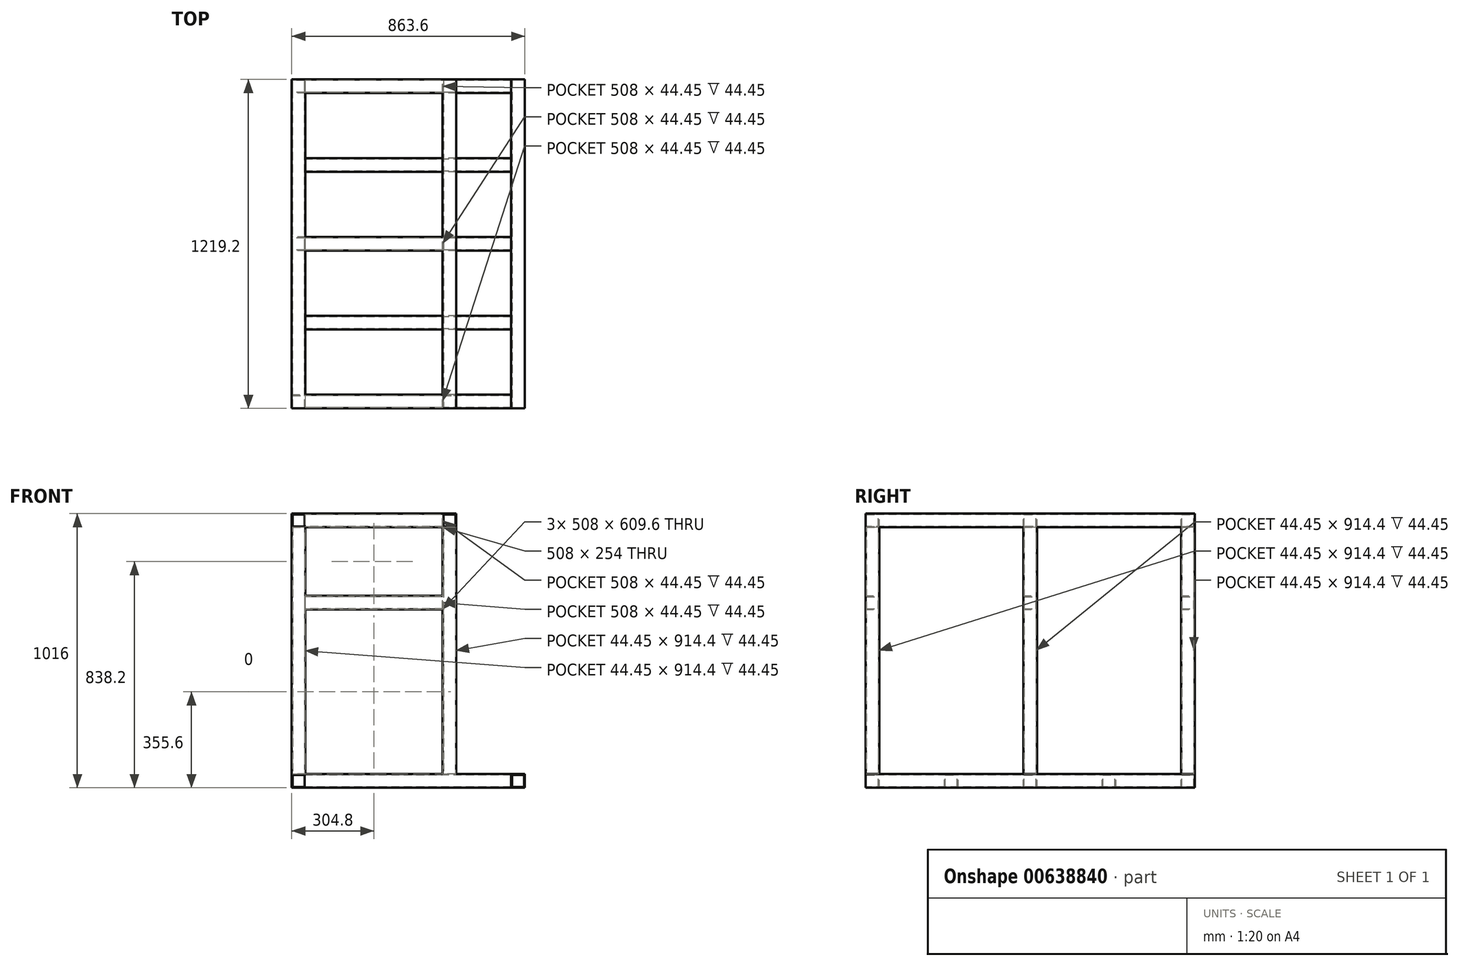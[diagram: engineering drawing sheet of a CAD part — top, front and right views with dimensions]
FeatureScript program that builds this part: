
annotation { "Feature Type Name" : "Feature", "Feature Type Description" : "" }
export const myFeature = defineFeature(function(context is Context, id is Id, definition is map)
    precondition{}
    {
        {
            var Q0;
            Q0=qCreatedBy(makeId("Front.planeOp"),FACE);
            var sketch = newSketch(context, id + "F0", { "sketchPlane" : qUnion([Q0])});
            skLineSegment(sketch, "E0.bottom", {"start": v(0, 0) * mm, "end": v(50.8, 0) * mm});
            skLineSegment(sketch, "E0.top", {"start": v(0, 50.8) * mm, "end": v(50.8, 50.8) * mm});
            skLineSegment(sketch, "E0.left", {"start": v(0, 0) * mm, "end": v(0, 50.8) * mm});
            skLineSegment(sketch, "E0.right", {"start": v(50.8, 0) * mm, "end": v(50.8, 50.8) * mm});
            skLineSegment(sketch, "E1.bottom", {"start": v(3.18, 3.17) * mm, "end": v(47.63, 3.17) * mm});
            skLineSegment(sketch, "E1.top", {"start": v(3.17, 47.63) * mm, "end": v(47.62, 47.63) * mm});
            skLineSegment(sketch, "E1.left", {"start": v(3.18, 3.18) * mm, "end": v(3.17, 47.63) * mm});
            skLineSegment(sketch, "E1.right", {"start": v(47.63, 3.18) * mm, "end": v(47.62, 47.63) * mm});
            skSolve(sketch);
        }
        {
            var Q0;
            Q0 = qSketchRegion(id + "F0", true);
            extrude(context, id + "F1", {"entities" : qUnion([Q0]), "depth" : 1219.2 * mm, "offsetDistance" : 25.4 * mm});
        }
        {
            var Q0;
            Q0=makeQuery(id+"F1.opExtrude","SWEPT_FACE",FACE,{"disambiguationData":[OSD([sQuery(id+"F0.wireOp",EDGE,"E0.right")])]});
            var sketch = newSketch(context, id + "F2", { "sketchPlane" : qUnion([Q0])});
            skLineSegment(sketch, "E2.bottom", {"start": v(-1219.2, 0) * mm, "end": v(-1168.4, 0) * mm});
            skLineSegment(sketch, "E2.top", {"start": v(-1219.2, 50.8) * mm, "end": v(-1168.4, 50.8) * mm});
            skLineSegment(sketch, "E2.left", {"start": v(-1219.2, 0) * mm, "end": v(-1219.2, 50.8) * mm});
            skLineSegment(sketch, "E2.right", {"start": v(-1168.4, 0) * mm, "end": v(-1168.4, 50.8) * mm});
            skLineSegment(sketch, "E3.0", {"start": v(-1171.57, 3.17) * mm, "end": v(-1171.57, 47.63) * mm});
            skLineSegment(sketch, "E3.1", {"start": v(-1216.03, 3.17) * mm, "end": v(-1171.57, 3.17) * mm});
            skLineSegment(sketch, "E3.2", {"start": v(-1216.03, 3.17) * mm, "end": v(-1216.03, 47.63) * mm});
            skLineSegment(sketch, "E3.3", {"start": v(-1216.03, 47.63) * mm, "end": v(-1171.57, 47.63) * mm});
            skLineSegment(sketch, "E4.direction1", {"start": v(-1219.2, 0) * mm, "end": v(-927.1, 0) * mm, "construction": true});
            skLineSegment(sketch, "E5.0.1.0", {"start": v(-923.93, 47.63) * mm, "end": v(-879.48, 47.63) * mm});
            skLineSegment(sketch, "E5.3.1.0", {"start": v(-923.93, 3.17) * mm, "end": v(-923.93, 47.63) * mm});
            skLineSegment(sketch, "E5.6.1.0", {"start": v(-923.93, 3.17) * mm, "end": v(-879.48, 3.17) * mm});
            skLineSegment(sketch, "E5.9.1.0", {"start": v(-927.1, 50.8) * mm, "end": v(-876.3, 50.8) * mm});
            skLineSegment(sketch, "E5.12.1.0", {"start": v(-927.1, 0) * mm, "end": v(-876.3, 0) * mm});
            skLineSegment(sketch, "E5.15.1.0", {"start": v(-879.48, 3.17) * mm, "end": v(-879.48, 47.63) * mm});
            skLineSegment(sketch, "E5.18.1.0", {"start": v(-876.3, 0) * mm, "end": v(-876.3, 50.8) * mm});
            skLineSegment(sketch, "E5.21.1.0", {"start": v(-927.1, 0) * mm, "end": v(-927.1, 50.8) * mm});
            skLineSegment(sketch, "E6.0.2.0", {"start": v(-631.83, 47.63) * mm, "end": v(-587.38, 47.63) * mm});
            skLineSegment(sketch, "E6.3.2.0", {"start": v(-631.83, 3.17) * mm, "end": v(-631.83, 47.63) * mm});
            skLineSegment(sketch, "E6.6.2.0", {"start": v(-631.83, 3.17) * mm, "end": v(-587.38, 3.17) * mm});
            skLineSegment(sketch, "E6.9.2.0", {"start": v(-635, 50.8) * mm, "end": v(-584.2, 50.8) * mm});
            skLineSegment(sketch, "E6.12.2.0", {"start": v(-635, 0) * mm, "end": v(-584.2, 0) * mm});
            skLineSegment(sketch, "E6.15.2.0", {"start": v(-587.38, 3.17) * mm, "end": v(-587.38, 47.63) * mm});
            skLineSegment(sketch, "E6.18.2.0", {"start": v(-584.2, 0) * mm, "end": v(-584.2, 50.8) * mm});
            skLineSegment(sketch, "E6.21.2.0", {"start": v(-635, 0) * mm, "end": v(-635, 50.8) * mm});
            skLineSegment(sketch, "E6.0.3.0", {"start": v(-339.73, 47.63) * mm, "end": v(-295.27, 47.63) * mm});
            skLineSegment(sketch, "E6.3.3.0", {"start": v(-339.73, 3.17) * mm, "end": v(-339.73, 47.63) * mm});
            skLineSegment(sketch, "E6.6.3.0", {"start": v(-339.73, 3.17) * mm, "end": v(-295.27, 3.17) * mm});
            skLineSegment(sketch, "E6.9.3.0", {"start": v(-342.9, 50.8) * mm, "end": v(-292.1, 50.8) * mm});
            skLineSegment(sketch, "E6.12.3.0", {"start": v(-342.9, 0) * mm, "end": v(-292.1, 0) * mm});
            skLineSegment(sketch, "E6.15.3.0", {"start": v(-295.27, 3.17) * mm, "end": v(-295.27, 47.63) * mm});
            skLineSegment(sketch, "E6.18.3.0", {"start": v(-292.1, 0) * mm, "end": v(-292.1, 50.8) * mm});
            skLineSegment(sketch, "E6.21.3.0", {"start": v(-342.9, 0) * mm, "end": v(-342.9, 50.8) * mm});
            skLineSegment(sketch, "E7.0.4.0", {"start": v(-47.63, 47.63) * mm, "end": v(-3.17, 47.63) * mm});
            skLineSegment(sketch, "E7.3.4.0", {"start": v(-47.63, 3.17) * mm, "end": v(-47.63, 47.63) * mm});
            skLineSegment(sketch, "E7.6.4.0", {"start": v(-47.63, 3.17) * mm, "end": v(-3.17, 3.17) * mm});
            skLineSegment(sketch, "E7.9.4.0", {"start": v(-50.8, 50.8) * mm, "end": v(0, 50.8) * mm});
            skLineSegment(sketch, "E7.12.4.0", {"start": v(-50.8, 0) * mm, "end": v(0, 0) * mm});
            skLineSegment(sketch, "E7.15.4.0", {"start": v(-3.17, 3.17) * mm, "end": v(-3.17, 47.63) * mm});
            skLineSegment(sketch, "E7.18.4.0", {"start": v(0, 0) * mm, "end": v(0, 50.8) * mm});
            skLineSegment(sketch, "E7.21.4.0", {"start": v(-50.8, 0) * mm, "end": v(-50.8, 50.8) * mm});
            skSolve(sketch);
        }
        {
            var Q0;
            Q0 = qSketchRegion(id + "F2", true);
            extrude(context, id + "F3", {"entities" : qUnion([Q0]), "operationType" : NewBodyOperationType.ADD, "depth" : 762 * mm, "offsetDistance" : 25.4 * mm});
        }
        {
            var Q0;
            Q0=makeQuery(id+"F3.boolean.opBoolean","MERGE",FACE,{"derivedFrom":[makeQuery(id+"F1.opExtrude","CAP_FACE",FACE,{"disambiguationData":[OSD([sQuery(id+"F0.wireOp",EDGE,"E0.bottom"),sQuery(id+"F0.wireOp",EDGE,"E0.top"),sQuery(id+"F0.wireOp",EDGE,"E0.left"),sQuery(id+"F0.wireOp",EDGE,"E0.right"),sQuery(id+"F0.wireOp",EDGE,"E1.bottom"),sQuery(id+"F0.wireOp",EDGE,"E1.top"),sQuery(id+"F0.wireOp",EDGE,"E1.left"),sQuery(id+"F0.wireOp",EDGE,"E1.right")])],"isStart":false}),makeQuery(id+"F3.opExtrude","SWEPT_FACE",FACE,{"disambiguationData":[OSD([sQuery(id+"F2.wireOp",EDGE,"E2.left")])]})]});
            var sketch = newSketch(context, id + "F4", { "sketchPlane" : qUnion([Q0])});
            skLineSegment(sketch, "E8.bottom", {"start": v(812.8, 0) * mm, "end": v(863.6, 0) * mm});
            skLineSegment(sketch, "E8.top", {"start": v(812.8, 50.8) * mm, "end": v(863.6, 50.8) * mm});
            skLineSegment(sketch, "E8.left", {"start": v(812.8, 0) * mm, "end": v(812.8, 50.8) * mm});
            skLineSegment(sketch, "E8.right", {"start": v(863.6, 0) * mm, "end": v(863.6, 50.8) * mm});
            skLineSegment(sketch, "E9.0", {"start": v(815.98, 3.18) * mm, "end": v(860.42, 3.18) * mm});
            skLineSegment(sketch, "E9.1", {"start": v(815.98, 3.18) * mm, "end": v(815.98, 47.62) * mm});
            skLineSegment(sketch, "E9.2", {"start": v(815.98, 47.62) * mm, "end": v(860.42, 47.62) * mm});
            skLineSegment(sketch, "E9.3", {"start": v(860.42, 3.18) * mm, "end": v(860.42, 47.62) * mm});
            skSolve(sketch);
        }
        {
            var Q0;
            Q0 = qSketchRegion(id + "F4", true);
            extrude(context, id + "F5", {"entities" : qUnion([Q0]), "oppositeDirection" : true, "depth" : 1219.2 * mm, "offsetDistance" : 25.4 * mm});
        }
        {
            var Q0;
            Q0=makeQuery(id+"F3.boolean.opBoolean","MERGE",FACE,{"derivedFrom":[makeQuery(id+"F1.opExtrude","SWEPT_FACE",FACE,{"disambiguationData":[OSD([sQuery(id+"F0.wireOp",EDGE,"E0.top")])]}),makeQuery(id+"F3.opExtrude","SWEPT_FACE",FACE,{"disambiguationData":[OSD([sQuery(id+"F2.wireOp",EDGE,"E2.top")])]}),makeQuery(id+"F3.opExtrude","SWEPT_FACE",FACE,{"disambiguationData":[OSD([sQuery(id+"F2.wireOp",EDGE,"E5.9.1.0")])]}),makeQuery(id+"F3.opExtrude","SWEPT_FACE",FACE,{"disambiguationData":[OSD([sQuery(id+"F2.wireOp",EDGE,"E6.9.2.0")])]}),makeQuery(id+"F3.opExtrude","SWEPT_FACE",FACE,{"disambiguationData":[OSD([sQuery(id+"F2.wireOp",EDGE,"E6.9.3.0")])]}),makeQuery(id+"F3.opExtrude","SWEPT_FACE",FACE,{"disambiguationData":[OSD([sQuery(id+"F2.wireOp",EDGE,"E7.9.4.0")])]})]});
            var sketch = newSketch(context, id + "F6", { "sketchPlane" : qUnion([Q0])});
            skLineSegment(sketch, "E10.bottom", {"start": v(0, -1219.2) * mm, "end": v(50.8, -1219.2) * mm});
            skLineSegment(sketch, "E10.top", {"start": v(0, -1168.4) * mm, "end": v(50.8, -1168.4) * mm});
            skLineSegment(sketch, "E10.left", {"start": v(0, -1219.2) * mm, "end": v(0, -1168.4) * mm});
            skLineSegment(sketch, "E10.right", {"start": v(50.8, -1219.2) * mm, "end": v(50.8, -1168.4) * mm});
            skLineSegment(sketch, "E11.bottom", {"start": v(50.8, -50.8) * mm, "end": v(0, -50.8) * mm});
            skLineSegment(sketch, "E11.top", {"start": v(50.8, 0) * mm, "end": v(0, 0) * mm});
            skLineSegment(sketch, "E11.left", {"start": v(50.8, -50.8) * mm, "end": v(50.8, 0) * mm});
            skLineSegment(sketch, "E11.right", {"start": v(0, -50.8) * mm, "end": v(0, 0) * mm});
            skLineSegment(sketch, "E12.bottom", {"start": v(50.8, -635) * mm, "end": v(0, -635) * mm});
            skLineSegment(sketch, "E12.top", {"start": v(50.8, -584.2) * mm, "end": v(0, -584.2) * mm});
            skLineSegment(sketch, "E12.left", {"start": v(50.8, -635) * mm, "end": v(50.8, -584.2) * mm});
            skLineSegment(sketch, "E12.right", {"start": v(0, -635) * mm, "end": v(0, -584.2) * mm});
            skLineSegment(sketch, "E13.0", {"start": v(3.17, -1171.58) * mm, "end": v(47.63, -1171.58) * mm});
            skLineSegment(sketch, "E13.1", {"start": v(3.17, -1216.03) * mm, "end": v(3.17, -1171.58) * mm});
            skLineSegment(sketch, "E13.2", {"start": v(3.17, -1216.03) * mm, "end": v(47.63, -1216.03) * mm});
            skLineSegment(sketch, "E13.3", {"start": v(47.63, -1216.03) * mm, "end": v(47.63, -1171.58) * mm});
            skLineSegment(sketch, "E14.0", {"start": v(3.18, -631.83) * mm, "end": v(3.17, -587.38) * mm});
            skLineSegment(sketch, "E14.1", {"start": v(47.63, -631.83) * mm, "end": v(3.18, -631.83) * mm});
            skLineSegment(sketch, "E14.2", {"start": v(47.63, -631.83) * mm, "end": v(47.62, -587.38) * mm});
            skLineSegment(sketch, "E14.3", {"start": v(47.62, -587.38) * mm, "end": v(3.17, -587.38) * mm});
            skLineSegment(sketch, "E15.0", {"start": v(47.63, -47.63) * mm, "end": v(3.18, -47.63) * mm});
            skLineSegment(sketch, "E15.1", {"start": v(47.63, -47.63) * mm, "end": v(47.62, -3.17) * mm});
            skLineSegment(sketch, "E15.2", {"start": v(47.62, -3.17) * mm, "end": v(3.17, -3.17) * mm});
            skLineSegment(sketch, "E15.3", {"start": v(3.18, -47.63) * mm, "end": v(3.17, -3.18) * mm});
            skLineSegment(sketch, "E16.1.0.0", {"start": v(558.8, -1219.2) * mm, "end": v(609.6, -1219.2) * mm});
            skLineSegment(sketch, "E16.1.0.1", {"start": v(561.97, -1216.03) * mm, "end": v(606.42, -1216.03) * mm});
            skLineSegment(sketch, "E16.1.0.2", {"start": v(609.6, 0) * mm, "end": v(558.8, 0) * mm});
            skLineSegment(sketch, "E16.1.0.3", {"start": v(606.42, -587.38) * mm, "end": v(561.97, -587.38) * mm});
            skLineSegment(sketch, "E16.1.0.4", {"start": v(606.42, -631.83) * mm, "end": v(561.97, -631.83) * mm});
            skLineSegment(sketch, "E16.1.0.5", {"start": v(606.42, -3.17) * mm, "end": v(561.97, -3.17) * mm});
            skLineSegment(sketch, "E16.1.0.6", {"start": v(609.6, -635) * mm, "end": v(609.6, -584.2) * mm});
            skLineSegment(sketch, "E16.1.0.7", {"start": v(609.6, -584.2) * mm, "end": v(558.8, -584.2) * mm});
            skLineSegment(sketch, "E16.1.0.8", {"start": v(609.6, -635) * mm, "end": v(558.8, -635) * mm});
            skLineSegment(sketch, "E16.1.0.9", {"start": v(558.8, -1168.4) * mm, "end": v(609.6, -1168.4) * mm});
            skLineSegment(sketch, "E16.1.0.10", {"start": v(609.6, -50.8) * mm, "end": v(558.8, -50.8) * mm});
            skLineSegment(sketch, "E16.1.0.11", {"start": v(561.97, -1171.58) * mm, "end": v(606.42, -1171.58) * mm});
            skLineSegment(sketch, "E16.1.0.12", {"start": v(606.42, -1216.03) * mm, "end": v(606.42, -1171.58) * mm});
            skLineSegment(sketch, "E16.1.0.13", {"start": v(558.8, -1219.2) * mm, "end": v(558.8, -1168.4) * mm});
            skLineSegment(sketch, "E16.1.0.14", {"start": v(609.6, -1219.2) * mm, "end": v(609.6, -1168.4) * mm});
            skLineSegment(sketch, "E16.1.0.15", {"start": v(609.6, -50.8) * mm, "end": v(609.6, 0) * mm});
            skLineSegment(sketch, "E16.1.0.16", {"start": v(558.8, -50.8) * mm, "end": v(558.8, 0) * mm});
            skLineSegment(sketch, "E16.1.0.17", {"start": v(561.97, -1216.03) * mm, "end": v(561.97, -1171.58) * mm});
            skLineSegment(sketch, "E16.1.0.18", {"start": v(606.42, -47.63) * mm, "end": v(606.42, -3.17) * mm});
            skLineSegment(sketch, "E16.1.0.19", {"start": v(561.97, -47.63) * mm, "end": v(561.97, -3.18) * mm});
            skLineSegment(sketch, "E16.1.0.20", {"start": v(606.42, -631.83) * mm, "end": v(606.42, -587.38) * mm});
            skLineSegment(sketch, "E16.1.0.21", {"start": v(606.42, -47.63) * mm, "end": v(561.97, -47.63) * mm});
            skLineSegment(sketch, "E16.1.0.22", {"start": v(558.8, -635) * mm, "end": v(558.8, -584.2) * mm});
            skLineSegment(sketch, "E16.1.0.23", {"start": v(561.97, -631.83) * mm, "end": v(561.97, -587.38) * mm});
            skLineSegment(sketch, "E16.direction1", {"start": v(0, -1219.2) * mm, "end": v(558.8, -1219.2) * mm, "construction": true});
            skSolve(sketch);
        }
        {
            var Q0;
            Q0 = qSketchRegion(id + "F6", true);
            extrude(context, id + "F7", {"entities" : qUnion([Q0]), "operationType" : NewBodyOperationType.ADD, "depth" : 914.4 * mm, "offsetDistance" : 25.4 * mm});
        }
        {
            var Q0;
            Q0=makeQuery(id+"F7.boolean.opBoolean","MERGE",FACE,{"derivedFrom":[makeQuery(id+"F3.boolean.opBoolean","MERGE",FACE,{"derivedFrom":[makeQuery(id+"F1.opExtrude","CAP_FACE",FACE,{"disambiguationData":[OSD([sQuery(id+"F0.wireOp",EDGE,"E0.bottom"),sQuery(id+"F0.wireOp",EDGE,"E0.top"),sQuery(id+"F0.wireOp",EDGE,"E0.left"),sQuery(id+"F0.wireOp",EDGE,"E0.right"),sQuery(id+"F0.wireOp",EDGE,"E1.bottom"),sQuery(id+"F0.wireOp",EDGE,"E1.top"),sQuery(id+"F0.wireOp",EDGE,"E1.left"),sQuery(id+"F0.wireOp",EDGE,"E1.right")])],"isStart":false}),makeQuery(id+"F3.opExtrude","SWEPT_FACE",FACE,{"disambiguationData":[OSD([sQuery(id+"F2.wireOp",EDGE,"E2.left")])]})]}),makeQuery(id+"F7.opExtrude","SWEPT_FACE",FACE,{"disambiguationData":[OSD([sQuery(id+"F6.wireOp",EDGE,"E10.bottom")])]}),makeQuery(id+"F7.opExtrude","SWEPT_FACE",FACE,{"disambiguationData":[OSD([sQuery(id+"F6.wireOp",EDGE,"E16.1.0.0")])]})]});
            var sketch = newSketch(context, id + "F8", { "sketchPlane" : qUnion([Q0])});
            skLineSegment(sketch, "E17.bottom", {"start": v(0, 965.2) * mm, "end": v(50.8, 965.2) * mm});
            skLineSegment(sketch, "E17.top", {"start": v(0, 1016) * mm, "end": v(50.8, 1016) * mm});
            skLineSegment(sketch, "E17.left", {"start": v(0, 965.2) * mm, "end": v(0, 1016) * mm});
            skLineSegment(sketch, "E17.right", {"start": v(50.8, 965.2) * mm, "end": v(50.8, 1016) * mm});
            skLineSegment(sketch, "E18.bottom", {"start": v(558.8, 965.2) * mm, "end": v(609.6, 965.2) * mm});
            skLineSegment(sketch, "E18.top", {"start": v(558.8, 1016) * mm, "end": v(609.6, 1016) * mm});
            skLineSegment(sketch, "E18.left", {"start": v(558.8, 965.2) * mm, "end": v(558.8, 1016) * mm});
            skLineSegment(sketch, "E18.right", {"start": v(609.6, 965.2) * mm, "end": v(609.6, 1016) * mm});
            skLineSegment(sketch, "E19.0", {"start": v(47.63, 968.38) * mm, "end": v(47.63, 1012.83) * mm});
            skLineSegment(sketch, "E19.1", {"start": v(3.17, 968.38) * mm, "end": v(47.63, 968.38) * mm});
            skLineSegment(sketch, "E19.2", {"start": v(3.17, 968.38) * mm, "end": v(3.17, 1012.83) * mm});
            skLineSegment(sketch, "E19.3", {"start": v(3.17, 1012.83) * mm, "end": v(47.62, 1012.83) * mm});
            skLineSegment(sketch, "E20.0", {"start": v(606.42, 968.38) * mm, "end": v(606.42, 1012.82) * mm});
            skLineSegment(sketch, "E20.1", {"start": v(561.97, 968.38) * mm, "end": v(606.42, 968.38) * mm});
            skLineSegment(sketch, "E20.2", {"start": v(561.97, 968.38) * mm, "end": v(561.97, 1012.82) * mm});
            skLineSegment(sketch, "E20.3", {"start": v(561.97, 1012.82) * mm, "end": v(606.42, 1012.82) * mm});
            skSolve(sketch);
        }
        {
            var Q0;
            Q0 = qSketchRegion(id + "F8", true);
            extrude(context, id + "F9", {"entities" : qUnion([Q0]), "operationType" : NewBodyOperationType.ADD, "oppositeDirection" : true, "depth" : 1219.2 * mm, "offsetDistance" : 25.4 * mm});
        }
        {
            var Q0;
            Q0=makeQuery(id+"F9.boolean.opBoolean","MERGE",FACE,{"derivedFrom":[makeQuery(id+"F7.opExtrude","SWEPT_FACE",FACE,{"disambiguationData":[OSD([sQuery(id+"F6.wireOp",EDGE,"E10.right")])]}),makeQuery(id+"F7.opExtrude","SWEPT_FACE",FACE,{"disambiguationData":[OSD([sQuery(id+"F6.wireOp",EDGE,"E11.left")])]}),makeQuery(id+"F7.opExtrude","SWEPT_FACE",FACE,{"disambiguationData":[OSD([sQuery(id+"F6.wireOp",EDGE,"E12.left")])]}),makeQuery(id+"F9.opExtrude","SWEPT_FACE",FACE,{"disambiguationData":[OSD([sQuery(id+"F8.wireOp",EDGE,"E17.right")])]})]});
            var sketch = newSketch(context, id + "F10", { "sketchPlane" : qUnion([Q0])});
            skLineSegment(sketch, "E21.bottom", {"start": v(-1219.2, 711.2) * mm, "end": v(-1168.4, 711.2) * mm});
            skLineSegment(sketch, "E21.top", {"start": v(-1219.2, 660.4) * mm, "end": v(-1168.4, 660.4) * mm});
            skLineSegment(sketch, "E21.left", {"start": v(-1219.2, 660.4) * mm, "end": v(-1219.2, 711.2) * mm});
            skLineSegment(sketch, "E21.right", {"start": v(-1168.4, 660.4) * mm, "end": v(-1168.4, 711.2) * mm});
            skLineSegment(sketch, "E22.0", {"start": v(-1216.03, 708.02) * mm, "end": v(-1171.58, 708.02) * mm});
            skLineSegment(sketch, "E22.1", {"start": v(-1216.03, 663.58) * mm, "end": v(-1216.03, 708.02) * mm});
            skLineSegment(sketch, "E22.2", {"start": v(-1216.03, 663.58) * mm, "end": v(-1171.58, 663.58) * mm});
            skLineSegment(sketch, "E22.3", {"start": v(-1171.58, 663.58) * mm, "end": v(-1171.58, 708.02) * mm});
            skLineSegment(sketch, "E23.0.1.0", {"start": v(-1216.03, 968.38) * mm, "end": v(-1216.03, 1012.82) * mm});
            skLineSegment(sketch, "E23.0.1.1", {"start": v(-1216.03, 968.38) * mm, "end": v(-1171.58, 968.38) * mm});
            skLineSegment(sketch, "E23.0.1.2", {"start": v(-1171.58, 968.38) * mm, "end": v(-1171.58, 1012.82) * mm});
            skLineSegment(sketch, "E23.0.1.3", {"start": v(-1168.4, 965.2) * mm, "end": v(-1168.4, 1016) * mm});
            skLineSegment(sketch, "E23.0.1.4", {"start": v(-1219.2, 965.2) * mm, "end": v(-1219.2, 1016) * mm});
            skLineSegment(sketch, "E23.0.1.5", {"start": v(-1219.2, 965.2) * mm, "end": v(-1168.4, 965.2) * mm});
            skLineSegment(sketch, "E23.0.1.6", {"start": v(-1216.03, 1012.82) * mm, "end": v(-1171.58, 1012.82) * mm});
            skLineSegment(sketch, "E23.0.1.7", {"start": v(-1219.2, 1016) * mm, "end": v(-1168.4, 1016) * mm});
            skLineSegment(sketch, "E23.1.0.0", {"start": v(-631.83, 663.58) * mm, "end": v(-631.83, 708.02) * mm});
            skLineSegment(sketch, "E23.1.0.1", {"start": v(-631.83, 663.58) * mm, "end": v(-587.38, 663.58) * mm});
            skLineSegment(sketch, "E23.1.0.2", {"start": v(-587.38, 663.58) * mm, "end": v(-587.38, 708.02) * mm});
            skLineSegment(sketch, "E23.1.0.3", {"start": v(-584.2, 660.4) * mm, "end": v(-584.2, 711.2) * mm});
            skLineSegment(sketch, "E23.1.0.4", {"start": v(-635, 660.4) * mm, "end": v(-635, 711.2) * mm});
            skLineSegment(sketch, "E23.1.0.5", {"start": v(-635, 660.4) * mm, "end": v(-584.2, 660.4) * mm});
            skLineSegment(sketch, "E23.1.0.6", {"start": v(-631.83, 708.02) * mm, "end": v(-587.38, 708.02) * mm});
            skLineSegment(sketch, "E23.1.0.7", {"start": v(-635, 711.2) * mm, "end": v(-584.2, 711.2) * mm});
            skLineSegment(sketch, "E23.1.1.0", {"start": v(-631.83, 968.38) * mm, "end": v(-631.83, 1012.82) * mm});
            skLineSegment(sketch, "E23.1.1.1", {"start": v(-631.83, 968.38) * mm, "end": v(-587.38, 968.38) * mm});
            skLineSegment(sketch, "E23.1.1.2", {"start": v(-587.38, 968.38) * mm, "end": v(-587.38, 1012.82) * mm});
            skLineSegment(sketch, "E23.1.1.3", {"start": v(-584.2, 965.2) * mm, "end": v(-584.2, 1016) * mm});
            skLineSegment(sketch, "E23.1.1.4", {"start": v(-635, 965.2) * mm, "end": v(-635, 1016) * mm});
            skLineSegment(sketch, "E23.1.1.5", {"start": v(-635, 965.2) * mm, "end": v(-584.2, 965.2) * mm});
            skLineSegment(sketch, "E23.1.1.6", {"start": v(-631.83, 1012.82) * mm, "end": v(-587.38, 1012.82) * mm});
            skLineSegment(sketch, "E23.1.1.7", {"start": v(-635, 1016) * mm, "end": v(-584.2, 1016) * mm});
            skLineSegment(sketch, "E23.2.0.0", {"start": v(-47.63, 663.58) * mm, "end": v(-47.63, 708.02) * mm});
            skLineSegment(sketch, "E23.2.0.1", {"start": v(-47.63, 663.58) * mm, "end": v(-3.18, 663.58) * mm});
            skLineSegment(sketch, "E23.2.0.2", {"start": v(-3.18, 663.58) * mm, "end": v(-3.18, 708.02) * mm});
            skLineSegment(sketch, "E23.2.0.3", {"start": v(0, 660.4) * mm, "end": v(0, 711.2) * mm});
            skLineSegment(sketch, "E23.2.0.4", {"start": v(-50.8, 660.4) * mm, "end": v(-50.8, 711.2) * mm});
            skLineSegment(sketch, "E23.2.0.5", {"start": v(-50.8, 660.4) * mm, "end": v(0, 660.4) * mm});
            skLineSegment(sketch, "E23.2.0.6", {"start": v(-47.63, 708.02) * mm, "end": v(-3.18, 708.02) * mm});
            skLineSegment(sketch, "E23.2.0.7", {"start": v(-50.8, 711.2) * mm, "end": v(0, 711.2) * mm});
            skLineSegment(sketch, "E23.2.1.0", {"start": v(-47.63, 968.38) * mm, "end": v(-47.63, 1012.82) * mm});
            skLineSegment(sketch, "E23.2.1.1", {"start": v(-47.63, 968.38) * mm, "end": v(-3.18, 968.38) * mm});
            skLineSegment(sketch, "E23.2.1.2", {"start": v(-3.18, 968.38) * mm, "end": v(-3.18, 1012.82) * mm});
            skLineSegment(sketch, "E23.2.1.3", {"start": v(0, 965.2) * mm, "end": v(0, 1016) * mm});
            skLineSegment(sketch, "E23.2.1.4", {"start": v(-50.8, 965.2) * mm, "end": v(-50.8, 1016) * mm});
            skLineSegment(sketch, "E23.2.1.5", {"start": v(-50.8, 965.2) * mm, "end": v(0, 965.2) * mm});
            skLineSegment(sketch, "E23.2.1.6", {"start": v(-47.63, 1012.82) * mm, "end": v(-3.18, 1012.82) * mm});
            skLineSegment(sketch, "E23.2.1.7", {"start": v(-50.8, 1016) * mm, "end": v(0, 1016) * mm});
            skLineSegment(sketch, "E23.direction1", {"start": v(-1219.2, 660.4) * mm, "end": v(-635, 660.4) * mm, "construction": true});
            skLineSegment(sketch, "E23.direction2", {"start": v(-1219.2, 660.4) * mm, "end": v(-1219.2, 965.2) * mm, "construction": true});
            skLineSegment(sketch, "E24.direction1", {"start": v(-1219.2, 965.2) * mm, "end": v(-635, 965.2) * mm, "construction": true});
            skSolve(sketch);
        }
        {
            var Q0;
            Q0 = qSketchRegion(id + "F10", true);
            extrude(context, id + "F11", {"entities" : qUnion([Q0]), "operationType" : NewBodyOperationType.ADD, "depth" : 508 * mm, "offsetDistance" : 25.4 * mm});
        }
    });
